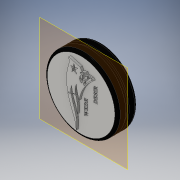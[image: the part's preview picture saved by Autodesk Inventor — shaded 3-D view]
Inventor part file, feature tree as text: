
AUTODESK INVENTOR PART (.ipt)
format: ipt  version: 2016 (Build 200138000, 138)  size: 966,656 bytes
history: native  units: in
note: dims shown in document units (in); Inventor stores cm internally (conversion verified against a paired STEP export)
features: extrude x17, sketch x15, fillet x3, plane x1, other x1
ambient origin geometry x8: Origin, YZ Plane, XZ Plane, XY Plane, X Axis, Y Axis, Z Axis, Center Point
bodies: Solid1 (feature_tree)
feature tree (37):
  extrude  "Extrusion1"  Depth=0.128in TaperAngle=0.0deg
  extrude  "Extrusion2"  Depth=0.3in TaperAngle=0.0deg
  sketch  "Sketch3"  dims[d3=2.65in d4=0.3in d5=0.0in d6=2.65in]
  fillet  "Fillet1"  Radius=2.65in
  extrude  "Extrusion3"  Depth=0.3in TaperAngle=0.0deg
  fillet  "Fillet2"  Radius=0.1in
  extrude  "Extrusion4"  Depth=0.046in TaperAngle=0.0deg
  extrude  "Extrusion5"  Depth=0.098in
  extrude  "Extrusion6"  Depth=0.2in
  extrude  "Extrusion7"  Depth=0.0844in
  extrude  "Extrusion11"  Depth=0.009in TaperAngle=0.0deg
  extrude  "Extrusion12"  Depth=0.085in
  extrude  "Extrusion13"  Depth=0.085in
  extrude  "Extrusion14"  Depth=0.1in TaperAngle=0.0deg
  fillet  "Fillet3"  Radius=0.6in
  extrude  "Extrusion15"  Depth=0.5in TaperAngle=0.0deg
  extrude  "Extrusion16"  Depth=1.5748in TaperAngle=360.0deg
  extrude  "Extrusion17"  Depth=0.4in TaperAngle=0.0deg
  plane  "Work Plane2"
  extrude  "Extrusion18"  Depth=0.17in
  extrude  "Extrusion19"  Depth=0.17in
  extrude  "Extrusion20"  Depth=0.17in
  sketch  "Sketch1"  dims[d0=2.5in d1=0.128in d2=0.0in]
  sketch  "Sketch4"  dims[d7=0.1in d8=0.3in d9=0.0in d10=0.1in]
  sketch  "Sketch5"  dims[d11=0.093in d12=0.0in d13=0.046in d14=0.0in]
  sketch  "Sketch7"  dims[d15=0.285in d16=0.098in]
  sketch  "Sketch12"  dims[d17=0.3in d18=0.0in d19=0.2in]
  sketch  "Sketch16"  dims[d41=0.2835in d42=0.009in d43=0.0in]
  sketch  "Sketch17"  dims[d46=0.085in d48=0.085in]
  sketch  "Sketch20"  dims[d49=0.085in d50=0.085in]
  sketch  "Sketch21"  dims[d51=0.5in d52=0.0in d53=0.1in d54=0.0in d56=0.6in]
  sketch  "Sketch23"  dims[d60=2.3in d61=0.5in d62=0.0in]
  sketch  "Sketch24"  dims[d63=0.125in d64=1.5748in d66=360.0deg]
  sketch  "Sketch25"  dims[d68=1.5748in d70=360.0deg d72=0.4in d73=0.0in]
  other  "Image1"
  sketch  "Sketch26"  dims[d74=0.17in d75=0.17in d76=0.17in d77=0.17in d78=0.01in d79=0.0in d80=0.5in d81=0.0in d83=0.1in d84=0.0in d111=0.08in d112=0.0in d113=0.3in d114=0.0in]
  sketch  "Sketch13"  dims[d20=0.6in d21=0.0in d40=0.0844in]
